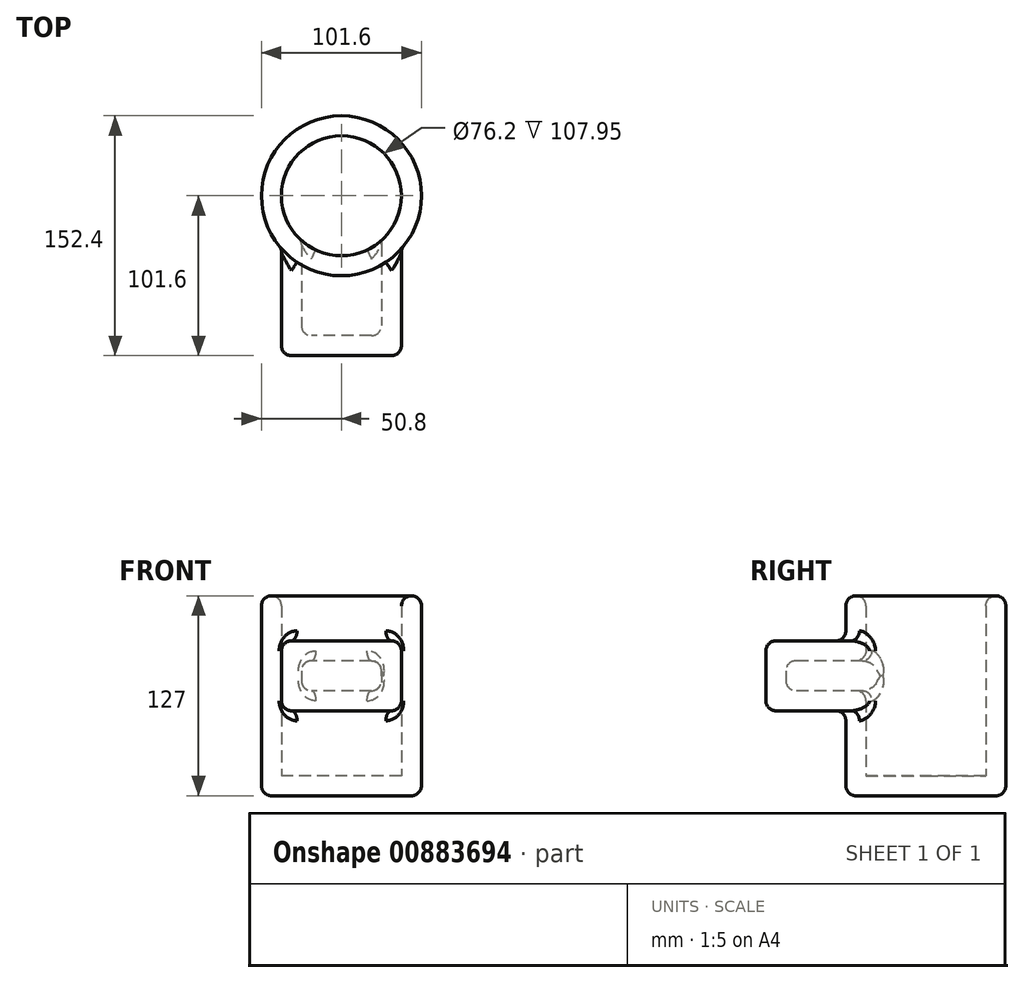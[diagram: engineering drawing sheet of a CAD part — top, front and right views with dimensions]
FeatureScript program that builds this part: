
annotation { "Feature Type Name" : "Feature", "Feature Type Description" : "" }
export const myFeature = defineFeature(function(context is Context, id is Id, definition is map)
    precondition{}
    {
        {
            var Q0;
            Q0=qCreatedBy(makeId("Top.planeOp"),FACE);
            var sketch = newSketch(context, id + "F0", { "sketchPlane" : qUnion([Q0])});
            skCircle(sketch, "E0", {"center": v(0, 0) * mm, "radius": 50.8 * mm});
            skSolve(sketch);
        }
        {
            var Q0;
            Q0=makeQuery(id+"F0.imprint","IMPRINT",FACE,{"disambiguationData":[TD([[makeQuery(id+"F0.imprint","IMPRINT",EDGE,{"derivedFrom":sQuery(id+"F0.wireOp",EDGE,"E0")}),1.0]])]});
            extrude(context, id + "F1", {"entities" : qUnion([Q0]), "depth" : 127 * mm, "offsetDistance" : 25.4 * mm});
        }
        {
            var Q0;
            Q0=qCreatedBy(makeId("Right.planeOp"),FACE);
            var sketch = newSketch(context, id + "F2", { "sketchPlane" : qUnion([Q0])});
            skLineSegment(sketch, "E1.bottom", {"start": v(0, 98.42) * mm, "end": v(-101.6, 98.42) * mm});
            skLineSegment(sketch, "E1.top", {"start": v(0, 53.98) * mm, "end": v(-101.6, 53.97) * mm});
            skLineSegment(sketch, "E1.left", {"start": v(0, 98.42) * mm, "end": v(0, 53.98) * mm});
            skLineSegment(sketch, "E1.right", {"start": v(-101.6, 98.42) * mm, "end": v(-101.6, 53.97) * mm});
            skLineSegment(sketch, "E2", {"start": v(0, 76.2) * mm, "end": v(-101.6, 76.2) * mm, "construction": true});
            skSolve(sketch);
        }
        {
            var Q0;
            Q0=makeQuery(id+"F2.imprint","IMPRINT",FACE,{"disambiguationData":[TD([[makeQuery(id+"F2.imprint","IMPRINT",EDGE,{"derivedFrom":sQuery(id+"F2.wireOp",EDGE,"E1.bottom")}),1.0]])]});
            extrude(context, id + "F3", {"entities" : qUnion([Q0]), "operationType" : NewBodyOperationType.ADD, "endBound" : BoundingType.SYMMETRIC, "depth" : 76.2 * mm, "offsetDistance" : 25.4 * mm});
        }
        {
            var Q0;
            Q0=makeQuery(id+"F1.opExtrude","CAP_FACE",FACE,{"disambiguationData":[OSD([sQuery(id+"F0.wireOp",EDGE,"E0")])],"isStart":false});
            shell(context, id + "F4", {"entities" : qUnion([Q0]), "thickness" : 12.7 * mm});
        }
        {
            var Q0;
            Q0=makeQuery(id+"F1.opExtrude","CAP_FACE",FACE,{"disambiguationData":[OSD([sQuery(id+"F0.wireOp",EDGE,"E0")])],"isStart":false});
            var Q1;
            Q1=makeQuery(id+"F1.opExtrude","SWEPT_FACE",FACE,{"disambiguationData":[OSD([sQuery(id+"F0.wireOp",EDGE,"E0")])]});
            var Q2;
            Q2=makeQuery(id+"F3.opExtrude","SWEPT_FACE",FACE,{"disambiguationData":[OSD([sQuery(id+"F2.wireOp",EDGE,"E1.bottom")])]});
            var Q3;
            Q3=makeQuery(id+"F3.opExtrude","SWEPT_FACE",FACE,{"disambiguationData":[OSD([sQuery(id+"F2.wireOp",EDGE,"E1.right")])]});
            var Q4;
            Q4=makeQuery(id+"F3.opExtrude","CAP_FACE",FACE,{"disambiguationData":[OSD([sQuery(id+"F2.wireOp",EDGE,"E1.bottom"),sQuery(id+"F2.wireOp",EDGE,"E1.top"),sQuery(id+"F2.wireOp",EDGE,"E1.left"),sQuery(id+"F2.wireOp",EDGE,"E1.right")])],"isStart":false});
            var Q5;
            Q5=makeQuery(id+"F3.opExtrude","CAP_FACE",FACE,{"disambiguationData":[OSD([sQuery(id+"F2.wireOp",EDGE,"E1.bottom"),sQuery(id+"F2.wireOp",EDGE,"E1.top"),sQuery(id+"F2.wireOp",EDGE,"E1.left"),sQuery(id+"F2.wireOp",EDGE,"E1.right")])],"isStart":true});
            var Q6;
            Q6=makeQuery(id+"F3.opExtrude","SWEPT_FACE",FACE,{"disambiguationData":[OSD([sQuery(id+"F2.wireOp",EDGE,"E1.top")])]});
            fillet(context, id + "F5", {"entities" : qUnion([Q0, Q1, Q2, Q3, Q4, Q5, Q6]), "radius" : 6.35 * mm, "tangentPropagation" : true, "defaultsChanged" : false, "vertexSettings" : [], "allowEdgeOverflow" : false});
        }
        {
            var Q0;
            Q0=makeQuery(id+"F4.opShell","OFFSET_FACE",FACE,{"disambiguationData":[OSD([sQuery(id+"F2.wireOp",EDGE,"E1.right")])]});
            var Q1;
            {var subQ0=sQuery(id+"F2.wireOp",EDGE,"E1.right");var subQ1=sQuery(id+"F2.wireOp",EDGE,"E1.left");var subQ2=sQuery(id+"F2.wireOp",EDGE,"E1.top");var subQ3=sQuery(id+"F2.wireOp",EDGE,"E1.bottom");Q1=makeQuery(id+"F4.opShell","OFFSET_FACE",FACE,{"disambiguationData":[OSD([subQ3,subQ2,subQ1,subQ0]),TDD([makeQuery(id+"F3.opExtrude","CAP_FACE",FACE,{"disambiguationData":[OSD([subQ3,subQ2,subQ1,subQ0])],"isStart":true})])]});}
            var Q2;
            Q2=makeQuery(id+"F4.opShell","OFFSET_FACE",FACE,{"disambiguationData":[OSD([sQuery(id+"F2.wireOp",EDGE,"E1.top")])]});
            var Q3;
            Q3=makeQuery(id+"F4.opShell","OFFSET_FACE",FACE,{"disambiguationData":[OSD([sQuery(id+"F2.wireOp",EDGE,"E1.bottom")])]});
            fillet(context, id + "F6", {"entities" : qUnion([Q0, Q1, Q2, Q3]), "radius" : 6.35 * mm, "tangentPropagation" : true, "allowEdgeOverflow" : false});
        }
    });
